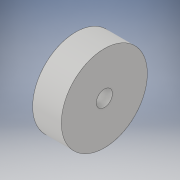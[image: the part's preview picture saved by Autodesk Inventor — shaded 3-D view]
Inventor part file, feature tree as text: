
AUTODESK INVENTOR PART (.ipt)
format: ipt  version: 2018 (Build 220112000, 112)  size: 96,256 bytes
history: native  units: in
note: dims shown in document units (in); Inventor stores cm internally (conversion verified against a paired STEP export)
features: extrude x1, sketch x1
ambient origin geometry x8: Origin, YZ Plane, XZ Plane, XY Plane, X Axis, Y Axis, Z Axis, Center Point
bodies: Solid1 (feature_tree)
feature tree (2):
  extrude  "Extrusion1"  Depth=2.0in
  sketch  "Sketch1"  dims[d0=6.0in d1=1.125in d2=2.0in d3=0.0in]
